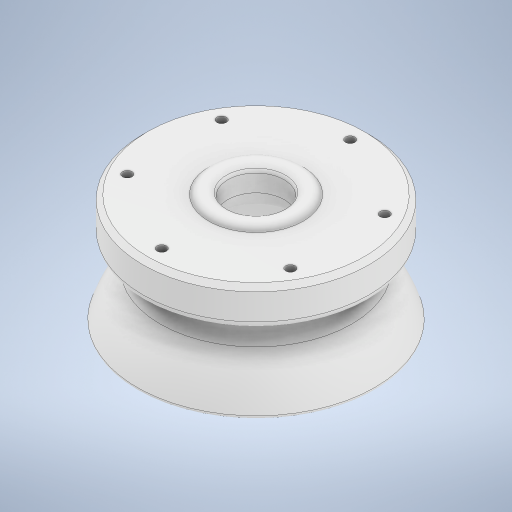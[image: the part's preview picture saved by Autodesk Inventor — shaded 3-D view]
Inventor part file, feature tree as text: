
AUTODESK INVENTOR PART (.ipt)
format: ipt  version: 2023 (Build 270158030, 158C)  size: 372,736 bytes
history: native  units: in
note: dims shown in document units (in); Inventor stores cm internally (conversion verified against a paired STEP export)
features: sketch x5, fillet x4, other x3, extrude x1, hole x1, pattern_circular x1, chamfer x1
ambient origin geometry x8: Origin, YZ Plane, XZ Plane, XY Plane, X Axis, Y Axis, Z Axis, Center Point
bodies: Solid1 (feature_tree)
feature tree (16):
  extrude  "Main-Body"  Depth=1.0in TaperAngle=0.0deg
  other  "Middle-Cutout"
  other  "Bump"
  fillet  "Fillet1"  Radius=1.0in
  other  "Dome-Support"
  fillet  "Fillet2"  [1 undecoded]
  fillet  "Fillet3"  Radius=0.3in
  fillet  "Fillet4"  Radius=0.5in
  hole  "Hole1"  [1 undecoded]
  pattern_circular  "Circular Pattern1"  [2 undecoded]
  chamfer  "Chamfer1"  Distance=0.25in
  sketch  "Sketch1"  dims[d0=6.0in d1=1.0in d2=0.0in d12=1.0in d13=360.0deg d15=0.3in d16=0.5in]
  sketch  "Sketch3"  dims[d17=360.0deg d18=0.125in]
  sketch  "Sketch4"  dims[d19=0.75in]
  sketch  "Sketch5"  dims[d20=0.25in d22=6.1in]
  sketch  "Sketch6"  dims[d28=360.0deg d29=6.1in d30=0.25in d31=0.4375in d32=0.0625in d33=0.1875in d34=0.252in d35=0.75in d36=0.375in d37=0.25in d38=0.5635in d39=0.4173in d40=0.0in d41=2.5in d42=2.3622in d43=360.0deg d45=0.125in d46=0.125in d47=45.0deg]
note: 4 required parameter values undecoded (feature->parameter linkage not recoverable at this tier; creation-order binding heuristic only, values carry confidence <= 0.55)
